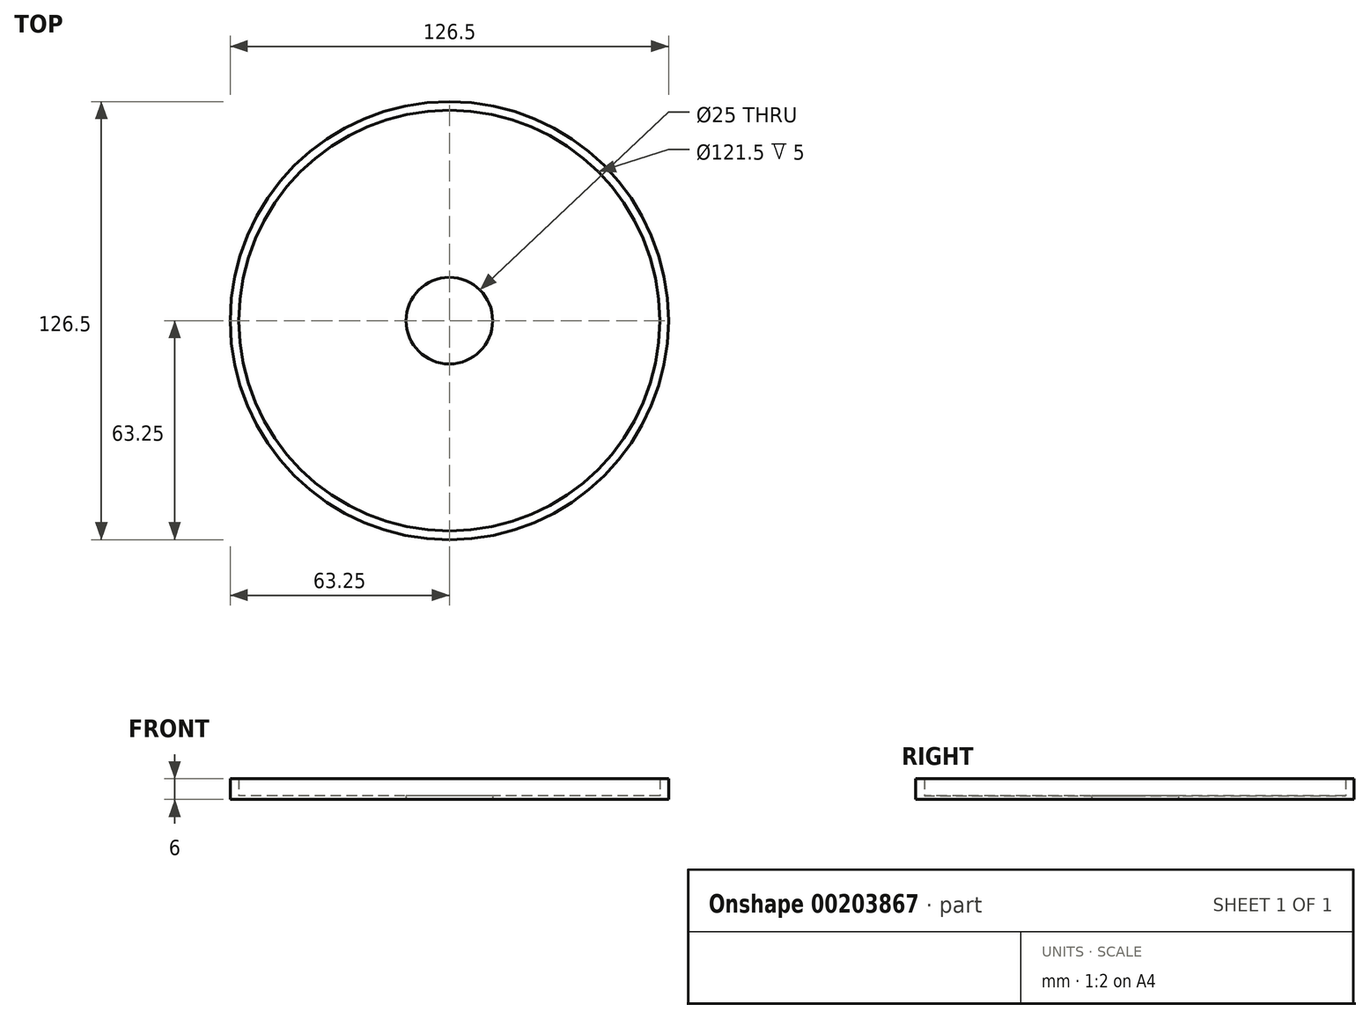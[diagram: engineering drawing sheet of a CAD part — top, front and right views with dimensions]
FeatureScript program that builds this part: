
annotation { "Feature Type Name" : "Feature", "Feature Type Description" : "" }
export const myFeature = defineFeature(function(context is Context, id is Id, definition is map)
    precondition{}
    {
        {
            var Q0;
            Q0=qCreatedBy(makeId("Top.planeOp"),FACE);
            var sketch = newSketch(context, id + "F0", { "sketchPlane" : qUnion([Q0])});
            skCircle(sketch, "E0", {"center": v(0, 0) * mm, "radius": 63.25 * mm});
            skCircle(sketch, "E1", {"center": v(0, 0) * mm, "radius": 12.5 * mm});
            skSolve(sketch);
        }
        {
            var Q0;
            Q0 = qSketchRegion(id + "F0", true);
            extrude(context, id + "F1", {"entities" : qUnion([Q0]), "depth" : 1 * mm});
        }
        {
            var Q0;
            Q0=makeQuery(id+"F1.opExtrude","CAP_FACE",FACE,{"disambiguationData":[OSD([sQuery(id+"F0.wireOp",EDGE,"E0")])],"isStart":false});
            var sketch = newSketch(context, id + "F2", { "sketchPlane" : qUnion([Q0])});
            skCircle(sketch, "E2", {"center": v(0, 0) * mm, "radius": 63.25 * mm});
            skCircle(sketch, "E3", {"center": v(0, 0) * mm, "radius": 60.75 * mm});
            skSolve(sketch);
        }
        {
            var Q0;
            Q0=makeQuery(id+"F2.imprint","IMPRINT",FACE,{"disambiguationData":[TD([[makeQuery(id+"F2.imprint","IMPRINT",EDGE,{"derivedFrom":sQuery(id+"F2.wireOp",EDGE,"E2")}),1.0]])]});
            extrude(context, id + "F3", {"entities" : qUnion([Q0]), "operationType" : NewBodyOperationType.ADD, "depth" : 5 * mm});
        }
    });
